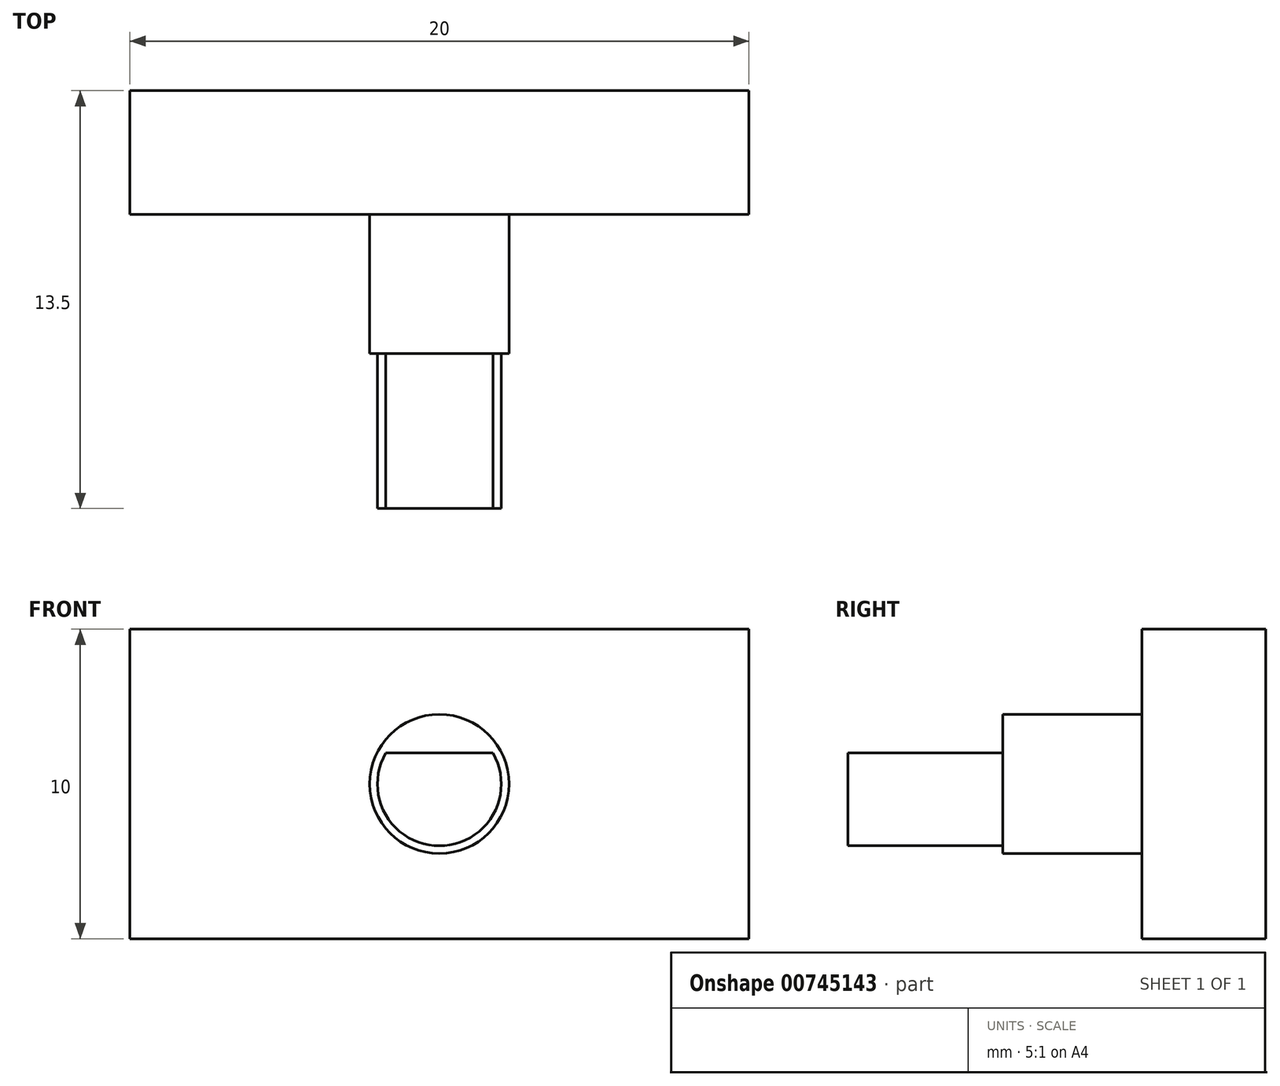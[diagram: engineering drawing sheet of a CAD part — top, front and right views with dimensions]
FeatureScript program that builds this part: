
annotation { "Feature Type Name" : "Feature", "Feature Type Description" : "" }
export const myFeature = defineFeature(function(context is Context, id is Id, definition is map)
    precondition{}
    {
        {
            var Q0;
            Q0=qCreatedBy(makeId("Front.planeOp"),FACE);
            var sketch = newSketch(context, id + "F0", { "sketchPlane" : qUnion([Q0])});
            skLineSegment(sketch, "E0.bottom", {"start": v(-10, 5) * mm, "end": v(10, 5) * mm});
            skLineSegment(sketch, "E0.top", {"start": v(-10, -5) * mm, "end": v(10, -5) * mm});
            skLineSegment(sketch, "E0.left", {"start": v(-10, 5) * mm, "end": v(-10, -5) * mm});
            skLineSegment(sketch, "E0.right", {"start": v(10, 5) * mm, "end": v(10, -5) * mm});
            skSolve(sketch);
        }
        {
            var Q0;
            Q0 = qSketchRegion(id + "F0", true);
            extrude(context, id + "F1", {"entities" : qUnion([Q0]), "depth" : 4 * mm, "offsetDistance" : 25 * mm});
        }
        {
            var Q0;
            Q0=makeQuery(id+"F1.opExtrude","CAP_FACE",FACE,{"disambiguationData":[OSD([sQuery(id+"F0.wireOp",EDGE,"E0.bottom"),sQuery(id+"F0.wireOp",EDGE,"E0.top"),sQuery(id+"F0.wireOp",EDGE,"E0.left"),sQuery(id+"F0.wireOp",EDGE,"E0.right")])],"isStart":false});
            var sketch = newSketch(context, id + "F2", { "sketchPlane" : qUnion([Q0])});
            skCircle(sketch, "E1", {"center": v(0, 0) * mm, "radius": 2.25 * mm});
            skSolve(sketch);
        }
        {
            var Q0;
            Q0 = qSketchRegion(id + "F2", true);
            extrude(context, id + "F3", {"entities" : qUnion([Q0]), "operationType" : NewBodyOperationType.ADD, "depth" : 4.5 * mm, "offsetDistance" : 25 * mm});
        }
        {
            var Q0;
            Q0=makeQuery(id+"F3.opExtrude","CAP_FACE",FACE,{"disambiguationData":[OSD([sQuery(id+"F2.wireOp",EDGE,"E1")])],"isStart":false});
            var sketch = newSketch(context, id + "F4", { "sketchPlane" : qUnion([Q0])});
            skCircle(sketch, "E2", {"center": v(0, 0) * mm, "radius": 2 * mm});
            skSolve(sketch);
        }
        {
            var Q0;
            Q0 = qSketchRegion(id + "F4", true);
            extrude(context, id + "F5", {"entities" : qUnion([Q0]), "operationType" : NewBodyOperationType.ADD, "depth" : 5 * mm, "offsetDistance" : 25 * mm});
        }
        {
            var Q0;
            Q0=makeQuery(id+"F5.opExtrude","CAP_FACE",FACE,{"disambiguationData":[OSD([sQuery(id+"F4.wireOp",EDGE,"E2")])],"isStart":false});
            var sketch = newSketch(context, id + "F6", { "sketchPlane" : qUnion([Q0])});
            skLineSegment(sketch, "E3", {"start": v(-1.73, 1) * mm, "end": v(1.73, 1) * mm});
            skArc(sketch, "E4", {"start": v(1.73, 1) * mm, "mid": v(0, 2) * mm, "end": v(-1.73, 1) * mm});
            skSolve(sketch);
        }
        {
            var Q0;
            Q0 = qSketchRegion(id + "F6", true);
            extrude(context, id + "F7", {"entities" : qUnion([Q0]), "operationType" : NewBodyOperationType.REMOVE, "oppositeDirection" : true, "depth" : 5 * mm, "offsetDistance" : 25 * mm});
        }
    });
